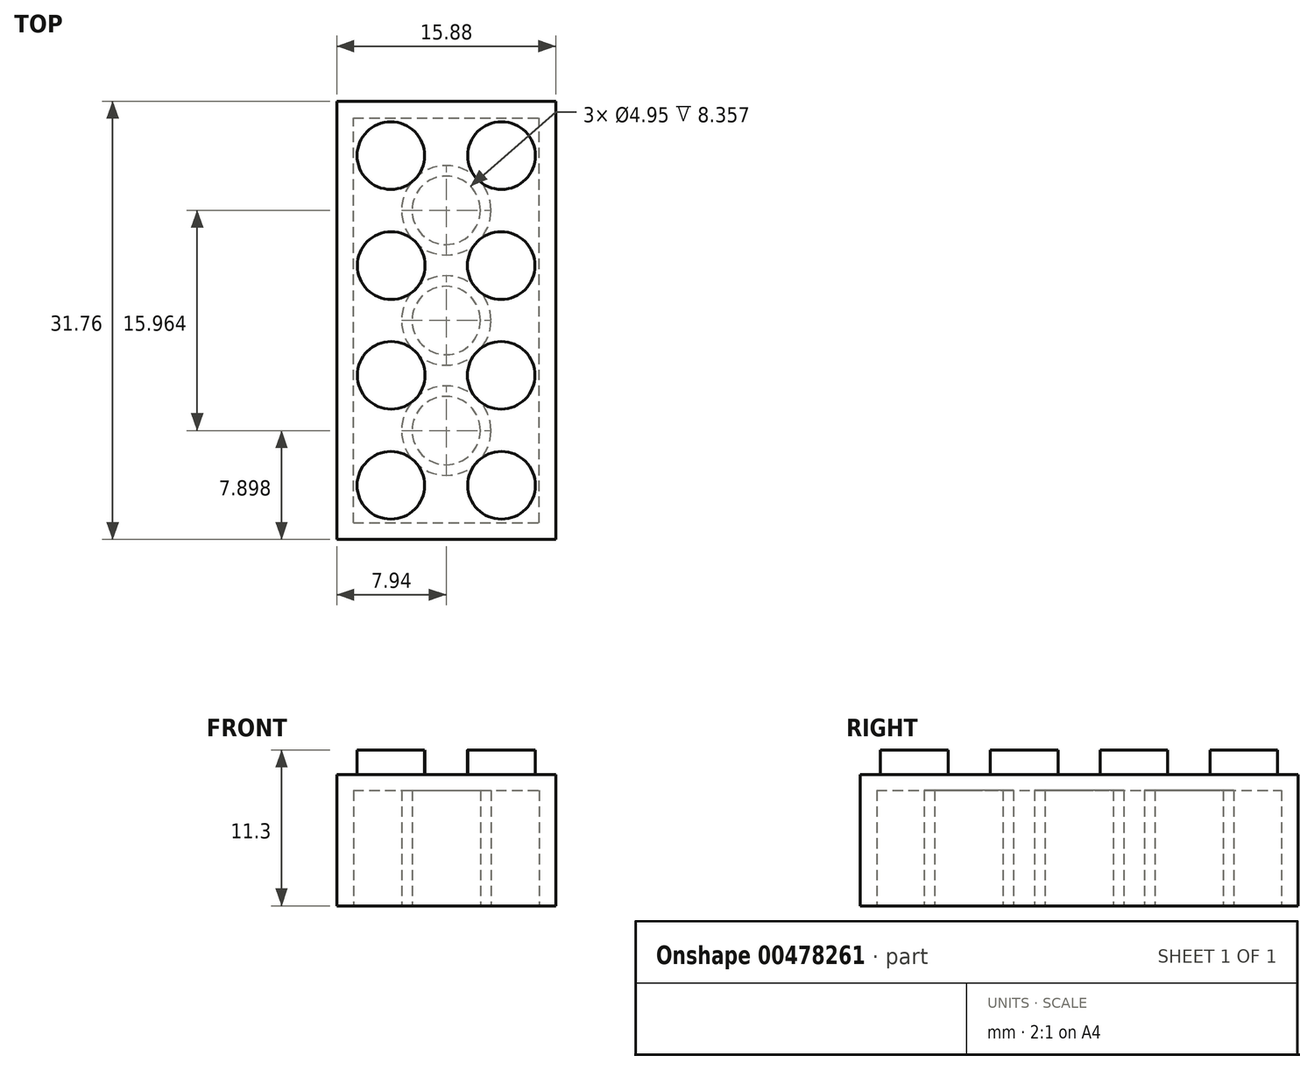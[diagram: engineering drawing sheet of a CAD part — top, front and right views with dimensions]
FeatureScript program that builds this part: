
annotation { "Feature Type Name" : "Feature", "Feature Type Description" : "" }
export const myFeature = defineFeature(function(context is Context, id is Id, definition is map)
    precondition{}
    {
        {
            var Q0;
            Q0=qCreatedBy(makeId("Top.planeOp"),FACE);
            var sketch = newSketch(context, id + "F0", { "sketchPlane" : qUnion([Q0])});
            skLineSegment(sketch, "E0.bottom", {"start": v(7.94, 15.87) * mm, "end": v(-7.94, 15.87) * mm});
            skLineSegment(sketch, "E0.top", {"start": v(7.94, -15.88) * mm, "end": v(-7.94, -15.88) * mm});
            skLineSegment(sketch, "E0.left", {"start": v(7.94, 15.88) * mm, "end": v(7.94, -15.88) * mm});
            skLineSegment(sketch, "E0.right", {"start": v(-7.94, 15.88) * mm, "end": v(-7.94, -15.88) * mm});
            skPoint(sketch, "E0.middle", {"position": v(0, 0) * mm});
            skSolve(sketch);
        }
        {
            var Q0;
            Q0 = qSketchRegion(id + "F0", true);
            extrude(context, id + "F1", {"entities" : qUnion([Q0]), "endBound" : BoundingType.SYMMETRIC, "depth" : 9.52 * mm});
        }
        {
            var Q0;
            Q0=makeQuery(id+"F1.opExtrude","CAP_FACE",FACE,{"disambiguationData":[OSD([sQuery(id+"F0.wireOp",EDGE,"E0.bottom"),sQuery(id+"F0.wireOp",EDGE,"E0.top"),sQuery(id+"F0.wireOp",EDGE,"E0.left"),sQuery(id+"F0.wireOp",EDGE,"E0.right")])],"isStart":false});
            var sketch = newSketch(context, id + "F2", { "sketchPlane" : qUnion([Q0])});
            skCircle(sketch, "E1", {"center": v(4.01, 11.95) * mm, "radius": 2.45 * mm});
            skCircle(sketch, "E2", {"center": v(-4.01, 11.95) * mm, "radius": 2.45 * mm});
            skCircle(sketch, "E3", {"center": v(-4.01, -11.95) * mm, "radius": 2.45 * mm});
            skCircle(sketch, "E4", {"center": v(4.01, -11.95) * mm, "radius": 2.45 * mm});
            skCircle(sketch, "E5", {"center": v(3.99, 3.98) * mm, "radius": 2.45 * mm});
            skCircle(sketch, "E6", {"center": v(3.99, -3.98) * mm, "radius": 2.45 * mm});
            skCircle(sketch, "E7", {"center": v(-3.99, 3.98) * mm, "radius": 2.45 * mm});
            skCircle(sketch, "E8", {"center": v(-3.99, -3.98) * mm, "radius": 2.45 * mm});
            skSolve(sketch);
        }
        {
            var Q0;
            Q0=makeQuery(id+"F2.imprint","IMPRINT",FACE,{"disambiguationData":[TD([[makeQuery(id+"F2.imprint","IMPRINT",EDGE,{"derivedFrom":sQuery(id+"F2.wireOp",EDGE,"E1")}),1.0]])]});
            var Q1;
            Q1=makeQuery(id+"F2.imprint","IMPRINT",FACE,{"disambiguationData":[TD([[makeQuery(id+"F2.imprint","IMPRINT",EDGE,{"derivedFrom":sQuery(id+"F2.wireOp",EDGE,"E5")}),1.0]])]});
            var Q2;
            Q2=makeQuery(id+"F2.imprint","IMPRINT",FACE,{"disambiguationData":[TD([[makeQuery(id+"F2.imprint","IMPRINT",EDGE,{"derivedFrom":sQuery(id+"F2.wireOp",EDGE,"E6")}),1.0]])]});
            var Q3;
            Q3=makeQuery(id+"F2.imprint","IMPRINT",FACE,{"disambiguationData":[TD([[makeQuery(id+"F2.imprint","IMPRINT",EDGE,{"derivedFrom":sQuery(id+"F2.wireOp",EDGE,"E4")}),1.0]])]});
            var Q4;
            Q4=makeQuery(id+"F2.imprint","IMPRINT",FACE,{"disambiguationData":[TD([[makeQuery(id+"F2.imprint","IMPRINT",EDGE,{"derivedFrom":sQuery(id+"F2.wireOp",EDGE,"E3")}),1.0]])]});
            var Q5;
            Q5=makeQuery(id+"F2.imprint","IMPRINT",FACE,{"disambiguationData":[TD([[makeQuery(id+"F2.imprint","IMPRINT",EDGE,{"derivedFrom":sQuery(id+"F2.wireOp",EDGE,"E8")}),1.0]])]});
            var Q6;
            Q6=makeQuery(id+"F2.imprint","IMPRINT",FACE,{"disambiguationData":[TD([[makeQuery(id+"F2.imprint","IMPRINT",EDGE,{"derivedFrom":sQuery(id+"F2.wireOp",EDGE,"E7")}),1.0]])]});
            var Q7;
            Q7=makeQuery(id+"F2.imprint","IMPRINT",FACE,{"disambiguationData":[TD([[makeQuery(id+"F2.imprint","IMPRINT",EDGE,{"derivedFrom":sQuery(id+"F2.wireOp",EDGE,"E2")}),1.0]])]});
            extrude(context, id + "F3", {"entities" : qUnion([Q0, Q1, Q2, Q3, Q4, Q5, Q6, Q7]), "operationType" : NewBodyOperationType.ADD, "depth" : 1.78 * mm});
        }
        {
            var Q0;
            Q0=makeQuery(id+"F1.opExtrude","CAP_FACE",FACE,{"disambiguationData":[OSD([sQuery(id+"F0.wireOp",EDGE,"E0.bottom"),sQuery(id+"F0.wireOp",EDGE,"E0.top"),sQuery(id+"F0.wireOp",EDGE,"E0.left"),sQuery(id+"F0.wireOp",EDGE,"E0.right")])],"isStart":true});
            var sketch = newSketch(context, id + "F4", { "sketchPlane" : qUnion([Q0])});
            skLineSegment(sketch, "E9.bottom", {"start": v(-6.73, 14.67) * mm, "end": v(6.73, 14.67) * mm});
            skLineSegment(sketch, "E9.top", {"start": v(-6.73, -14.67) * mm, "end": v(6.73, -14.67) * mm});
            skLineSegment(sketch, "E9.left", {"start": v(-6.73, 14.67) * mm, "end": v(-6.73, -14.67) * mm});
            skLineSegment(sketch, "E9.right", {"start": v(6.73, 14.67) * mm, "end": v(6.73, -14.67) * mm});
            skPoint(sketch, "E9.middle", {"position": v(0, 0) * mm});
            skCircle(sketch, "E10", {"center": v(0, 0) * mm, "radius": 3.24 * mm});
            skCircle(sketch, "E11", {"center": v(0, 7.98) * mm, "radius": 3.24 * mm});
            skCircle(sketch, "E12", {"center": v(0, -7.98) * mm, "radius": 3.24 * mm});
            skCircle(sketch, "E13", {"center": v(0, 0) * mm, "radius": 2.48 * mm});
            skCircle(sketch, "E14", {"center": v(0, 7.98) * mm, "radius": 2.48 * mm});
            skCircle(sketch, "E15", {"center": v(0, -7.98) * mm, "radius": 2.48 * mm});
            skSolve(sketch);
        }
        {
            var Q0;
            Q0=makeQuery(id+"F4.imprint","IMPRINT",FACE,{"disambiguationData":[TD([[makeQuery(id+"F4.imprint","IMPRINT",EDGE,{"derivedFrom":sQuery(id+"F4.wireOp",EDGE,"E9.bottom")}),-1.0]])]});
            extrude(context, id + "F5", {"entities" : qUnion([Q0]), "operationType" : NewBodyOperationType.REMOVE, "oppositeDirection" : true, "depth" : 8.36 * mm});
        }
        {
            var Q0;
            Q0=makeQuery(id+"F5.boolean.opBoolean","SPLIT",FACE,{"disambiguationData":[TD([makeQuery(id+"F5.opExtrude","SWEPT_FACE",FACE,{"disambiguationData":[OSD([sQuery(id+"F4.wireOp",EDGE,"E10")])]})])],"derivedFrom":makeQuery(id+"F1.opExtrude","CAP_FACE",FACE,{"disambiguationData":[OSD([sQuery(id+"F0.wireOp",EDGE,"E0.bottom"),sQuery(id+"F0.wireOp",EDGE,"E0.top"),sQuery(id+"F0.wireOp",EDGE,"E0.left"),sQuery(id+"F0.wireOp",EDGE,"E0.right")])],"isStart":true})});
            var sketch = newSketch(context, id + "F6", { "sketchPlane" : qUnion([Q0])});
            skCircle(sketch, "E16", {"center": v(0, 0) * mm, "radius": 2.48 * mm});
            skSolve(sketch);
        }
        {
            var Q0;
            Q0=makeQuery(id+"F5.boolean.opBoolean","SPLIT",FACE,{"disambiguationData":[TD([makeQuery(id+"F5.opExtrude","SWEPT_FACE",FACE,{"disambiguationData":[OSD([sQuery(id+"F4.wireOp",EDGE,"E11")])]})])],"derivedFrom":makeQuery(id+"F1.opExtrude","CAP_FACE",FACE,{"disambiguationData":[OSD([sQuery(id+"F0.wireOp",EDGE,"E0.bottom"),sQuery(id+"F0.wireOp",EDGE,"E0.top"),sQuery(id+"F0.wireOp",EDGE,"E0.left"),sQuery(id+"F0.wireOp",EDGE,"E0.right")])],"isStart":true})});
            var sketch = newSketch(context, id + "F7", { "sketchPlane" : qUnion([Q0])});
            skCircle(sketch, "E17", {"center": v(0, 7.98) * mm, "radius": 2.48 * mm});
            skSolve(sketch);
        }
        {
            var Q0;
            Q0=makeQuery(id+"F5.boolean.opBoolean","SPLIT",FACE,{"disambiguationData":[TD([makeQuery(id+"F5.opExtrude","SWEPT_FACE",FACE,{"disambiguationData":[OSD([sQuery(id+"F4.wireOp",EDGE,"E12")])]})])],"derivedFrom":makeQuery(id+"F1.opExtrude","CAP_FACE",FACE,{"disambiguationData":[OSD([sQuery(id+"F0.wireOp",EDGE,"E0.bottom"),sQuery(id+"F0.wireOp",EDGE,"E0.top"),sQuery(id+"F0.wireOp",EDGE,"E0.left"),sQuery(id+"F0.wireOp",EDGE,"E0.right")])],"isStart":true})});
            var sketch = newSketch(context, id + "F8", { "sketchPlane" : qUnion([Q0])});
            skCircle(sketch, "E18", {"center": v(0, -7.98) * mm, "radius": 2.48 * mm});
            skSolve(sketch);
        }
        {
            var Q0;
            Q0=makeQuery(id+"F6.imprint","IMPRINT",FACE,{"disambiguationData":[TD([[makeQuery(id+"F6.imprint","IMPRINT",EDGE,{"derivedFrom":sQuery(id+"F6.wireOp",EDGE,"E16")}),1.0]])]});
            var Q1;
            Q1=makeQuery(id+"F7.imprint","IMPRINT",FACE,{"disambiguationData":[TD([[makeQuery(id+"F7.imprint","IMPRINT",EDGE,{"derivedFrom":sQuery(id+"F7.wireOp",EDGE,"E17")}),1.0]])]});
            var Q2;
            Q2=makeQuery(id+"F8.imprint","IMPRINT",FACE,{"disambiguationData":[TD([[makeQuery(id+"F8.imprint","IMPRINT",EDGE,{"derivedFrom":sQuery(id+"F8.wireOp",EDGE,"E18")}),1.0]])]});
            extrude(context, id + "F9", {"entities" : qUnion([Q0, Q1, Q2]), "operationType" : NewBodyOperationType.REMOVE, "oppositeDirection" : true, "depth" : 8.36 * mm});
        }
    });
